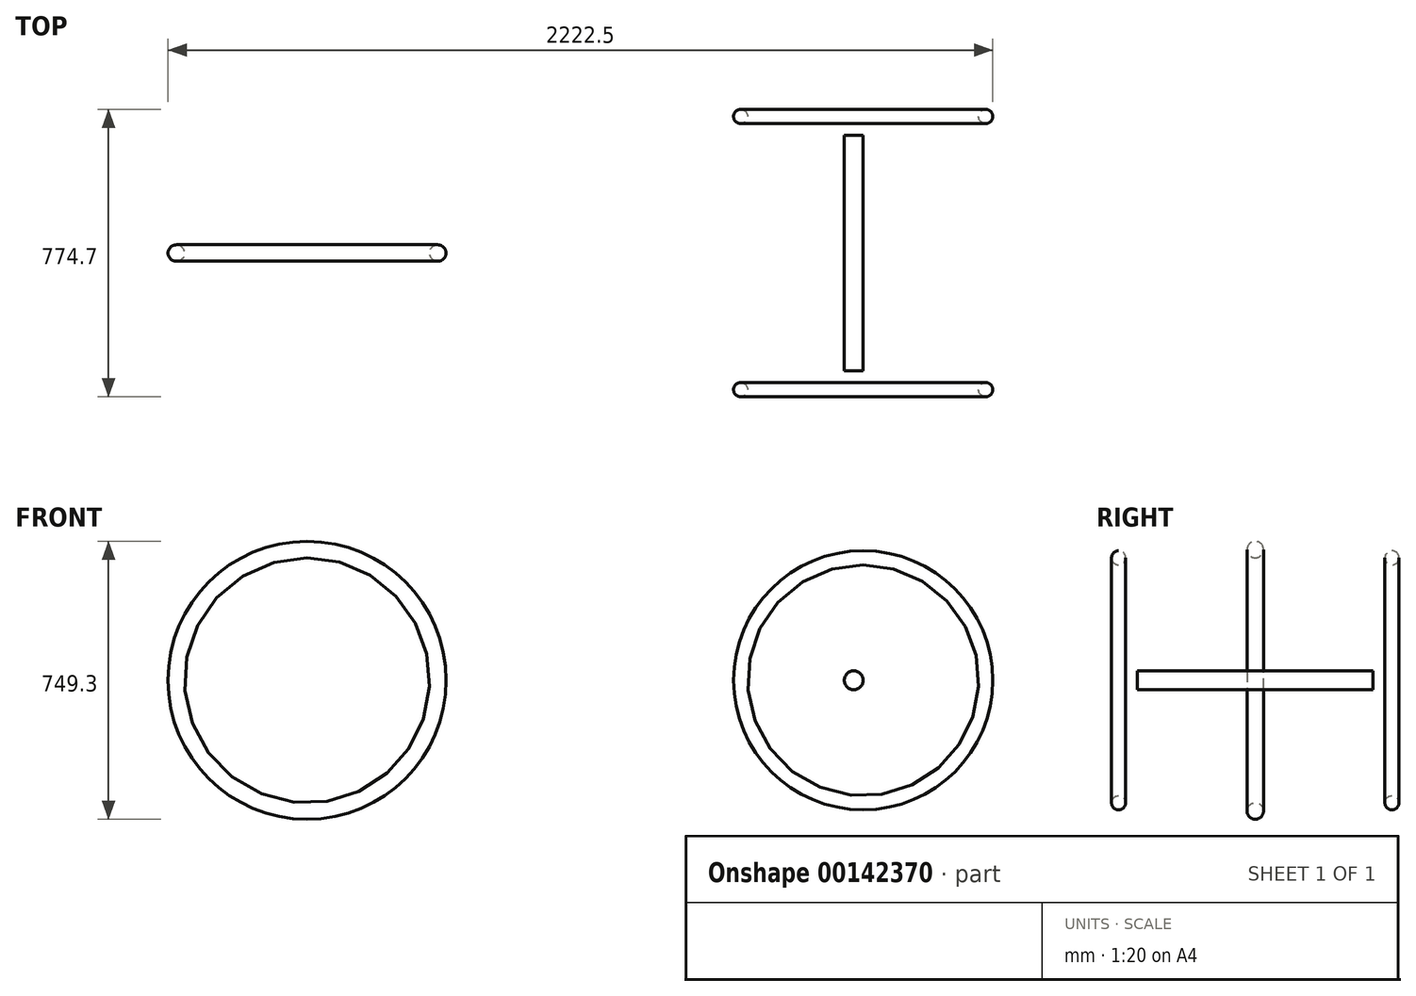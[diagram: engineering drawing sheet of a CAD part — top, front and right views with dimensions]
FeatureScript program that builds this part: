
annotation { "Feature Type Name" : "Feature", "Feature Type Description" : "" }
export const myFeature = defineFeature(function(context is Context, id is Id, definition is map)
    precondition{}
    {
        {
            var Q0;
            Q0=qCreatedBy(makeId("Right.planeOp"),FACE);
            var sketch = newSketch(context, id + "F0", { "sketchPlane" : qUnion([Q0])});
            skCircle(sketch, "E0", {"center": v(0, 352.43) * mm, "radius": 22.23 * mm});
            skLineSegment(sketch, "E1", {"start": v(0, 0) * mm, "end": v(-171.3, 0) * mm});
            skSolve(sketch);
        }
        {
            var Q0;
            Q0=makeQuery(id+"F0.imprint","IMPRINT",FACE,{"disambiguationData":[TD([[makeQuery(id+"F0.imprint","IMPRINT",EDGE,{"derivedFrom":sQuery(id+"F0.wireOp",EDGE,"E0")}),1.0]])]});
            var Q1;
            Q1=sQuery(id+"F0.wireOp",EDGE,"E1");
            revolve(context, id + "F1", {"entities" : qUnion([Q0]), "axis" : qUnion([Q1]), "revolveType" : RevolveType.FULL});
        }
        {
            var Q0;
            Q0=qCreatedBy(makeId("Front.planeOp"),FACE);
            var sketch = newSketch(context, id + "F2", { "sketchPlane" : qUnion([Q0])});
            skCircle(sketch, "E2", {"center": v(1473.2, 0) * mm, "radius": 25.4 * mm});
            skSolve(sketch);
        }
        {
            var Q0;
            Q0=makeQuery(id+"F2.imprint","IMPRINT",FACE,{"disambiguationData":[TD([[makeQuery(id+"F2.imprint","IMPRINT",EDGE,{"derivedFrom":sQuery(id+"F2.wireOp",EDGE,"E2")}),1.0]])]});
            extrude(context, id + "F3", {"entities" : qUnion([Q0]), "endBound" : BoundingType.SYMMETRIC, "depth" : 635 * mm});
        }
        {
            var Q0;
            Q0=qCreatedBy(makeId("Right.planeOp"),FACE);
            cPlane(context, id + "F4", {"entities" : qUnion([Q0]), "cplaneType" : CPlaneType.OFFSET, "offset" : 1498.6 * mm, "width" : 152.4 * mm, "height" : 152.4 * mm});
        }
        {
            var Q0;
            Q0=qCreatedBy(id+"F4.planeOp",FACE);
            var sketch = newSketch(context, id + "F5", { "sketchPlane" : qUnion([Q0])});
            skCircle(sketch, "E3", {"center": v(-368.3, 330.2) * mm, "radius": 19.05 * mm});
            skCircle(sketch, "E4", {"center": v(368.3, 330.2) * mm, "radius": 19.05 * mm});
            skLineSegment(sketch, "E5.0", {"start": v(-317.5, -25.4) * mm, "end": v(-317.5, 25.4) * mm});
            skLineSegment(sketch, "E6.0", {"start": v(317.5, -25.4) * mm, "end": v(317.5, 25.4) * mm});
            skLineSegment(sketch, "E7", {"start": v(0, 0) * mm, "end": v(-588.99, 0) * mm});
            skSolve(sketch);
        }
        {
            var Q0;
            Q0=makeQuery(id+"F5.imprint","IMPRINT",FACE,{"disambiguationData":[TD([[makeQuery(id+"F5.imprint","IMPRINT",EDGE,{"derivedFrom":sQuery(id+"F5.wireOp",EDGE,"E4")}),1.0]])]});
            var Q1;
            Q1=makeQuery(id+"F5.imprint","IMPRINT",FACE,{"disambiguationData":[TD([[makeQuery(id+"F5.imprint","IMPRINT",EDGE,{"derivedFrom":sQuery(id+"F5.wireOp",EDGE,"E3")}),1.0]])]});
            var Q2;
            Q2=sQuery(id+"F5.wireOp",EDGE,"E7");
            revolve(context, id + "F6", {"entities" : qUnion([Q0, Q1]), "axis" : qUnion([Q2]), "revolveType" : RevolveType.FULL});
        }
    });
